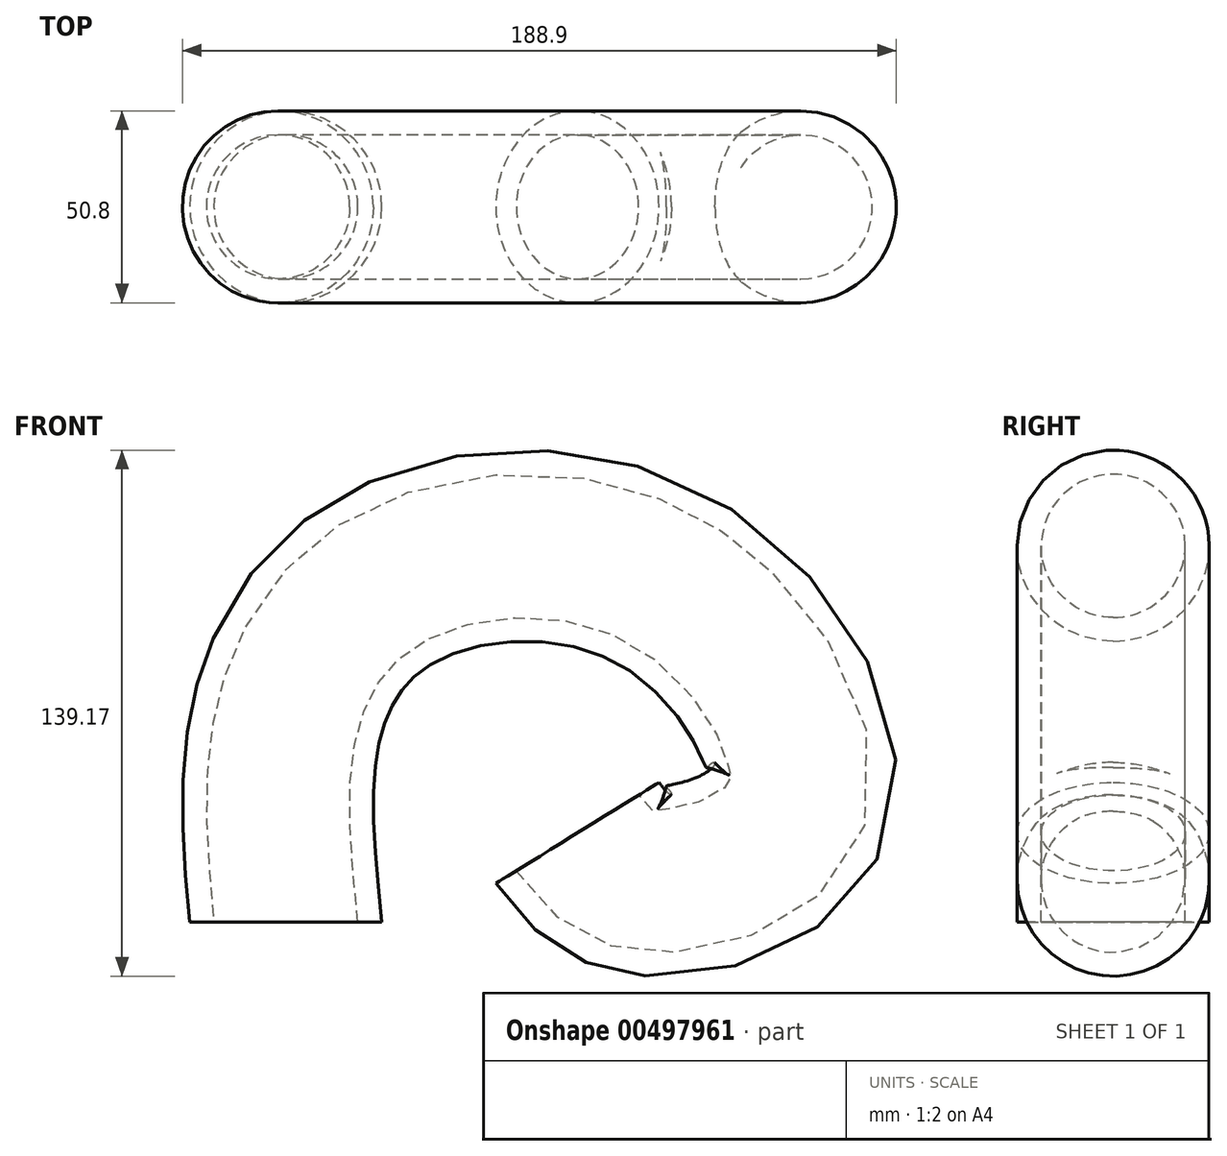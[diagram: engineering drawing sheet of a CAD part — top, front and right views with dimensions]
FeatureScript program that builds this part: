
annotation { "Feature Type Name" : "Feature", "Feature Type Description" : "" }
export const myFeature = defineFeature(function(context is Context, id is Id, definition is map)
    precondition{}
    {
        {
            var Q0;
            Q0=qCreatedBy(makeId("Top.planeOp"),FACE);
            var sketch = newSketch(context, id + "F0", { "sketchPlane" : qUnion([Q0])});
            skCircle(sketch, "E0", {"center": v(0, 0) * mm, "radius": 19.05 * mm});
            skCircle(sketch, "E1", {"center": v(0, 0) * mm, "radius": 25.4 * mm});
            skSolve(sketch);
        }
        {
            var Q0;
            Q0=qCreatedBy(makeId("Front.planeOp"),FACE);
            var sketch = newSketch(context, id + "F1", { "sketchPlane" : qUnion([Q0])});
            skFitSpline(sketch, "E2", {"points": [v(0, 0) * mm, v(0, 52.57) * mm, v(27.23, 90.82) * mm, v(102.23, 89.18) * mm, v(134.3, 29.08) * mm, v(93.8, 11.44) * mm, v(77.14, 23.58) * mm], "startDerivative": vector(-31.64, 315.41) * mm, "endDerivative": vector(-113.82, 148.46) * mm});
            skSolve(sketch);
        }
        {
            var Q0;
            Q0=makeQuery(id+"F0.imprint","IMPRINT",FACE,{"disambiguationData":[TD([[makeQuery(id+"F0.imprint","IMPRINT",EDGE,{"derivedFrom":sQuery(id+"F0.wireOp",EDGE,"E0")}),-1.0]])]});
            var Q1;
            Q1=sQuery(id+"F1.wireOp",EDGE,"E2");
            sweep(context, id + "F2", {"profiles" : qUnion([Q0]), "path" : qUnion([Q1])});
        }
    });
